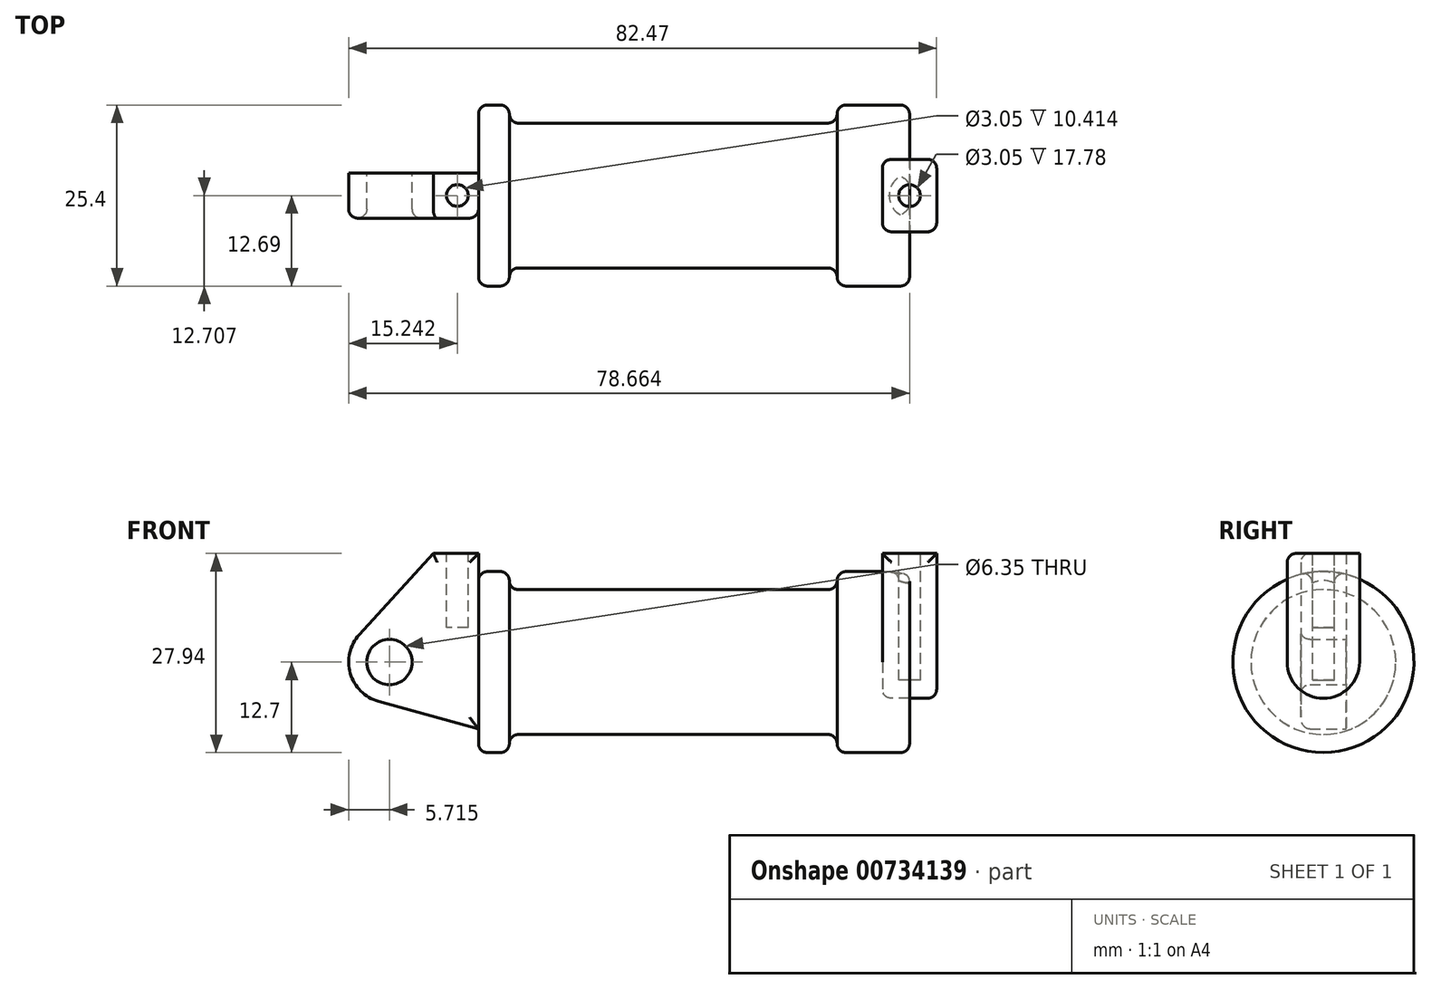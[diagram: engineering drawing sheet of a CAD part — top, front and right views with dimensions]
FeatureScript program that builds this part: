
annotation { "Feature Type Name" : "Feature", "Feature Type Description" : "" }
export const myFeature = defineFeature(function(context is Context, id is Id, definition is map)
    precondition{}
    {
        {
            var Q0;
            Q0=qCreatedBy(makeId("Front.planeOp"),FACE);
            var sketch = newSketch(context, id + "F0", { "sketchPlane" : qUnion([Q0])});
            skLineSegment(sketch, "E0", {"start": v(0, 0) * mm, "end": v(0, 12.7) * mm});
            skLineSegment(sketch, "E1", {"start": v(0, 12.7) * mm, "end": v(10.16, 12.7) * mm});
            skLineSegment(sketch, "E2", {"start": v(10.16, 12.7) * mm, "end": v(10.16, 10.16) * mm});
            skLineSegment(sketch, "E3", {"start": v(10.16, 10.16) * mm, "end": v(56.13, 10.16) * mm});
            skLineSegment(sketch, "E4", {"start": v(56.13, 10.16) * mm, "end": v(56.13, 12.7) * mm});
            skLineSegment(sketch, "E5", {"start": v(56.13, 12.7) * mm, "end": v(66.3, 12.7) * mm});
            skLineSegment(sketch, "E6", {"start": v(66.3, 12.7) * mm, "end": v(66.3, 0) * mm});
            skLineSegment(sketch, "E7", {"start": v(66.3, 0) * mm, "end": v(0, 0) * mm});
            skLineSegment(sketch, "E8", {"start": v(5.84, 15.24) * mm, "end": v(-0.5, 15.24) * mm});
            skLineSegment(sketch, "E9", {"start": v(-0.5, 15.24) * mm, "end": v(-10.88, 3.85) * mm});
            skLineSegment(sketch, "E10", {"start": v(0, 0) * mm, "end": v(-6.65, 0) * mm});
            skCircle(sketch, "E11", {"center": v(-6.65, 0) * mm, "radius": 5.72 * mm});
            skCircle(sketch, "E12", {"center": v(-6.65, 0) * mm, "radius": 3.18 * mm});
            skLineSegment(sketch, "E13", {"start": v(5.84, 15.24) * mm, "end": v(5.84, -9.4) * mm});
            skLineSegment(sketch, "E14", {"start": v(5.84, -9.4) * mm, "end": v(-8.18, -5.5) * mm});
            skSolve(sketch);
        }
        {
            var Q0;
            {var subQ0=sQuery(id+"F0.wireOp",EDGE,"E2");Q0=makeQuery(id+"F0.imprint","IMPRINT",FACE,{"disambiguationData":[TD([[makeQuery(id+"F0.imprint","IMPRINT",EDGE,{"derivedFrom":subQ0}),-1.0]])]});}
            var Q1;
            Q1=sQuery(id+"F0.wireOp",EDGE,"E7");
            revolve(context, id + "F1", {"surfaceOperationType" : NewSurfaceOperationType.NEW, "entities" : qUnion([Q0]), "axis" : qUnion([Q1]), "revolveType" : RevolveType.FULL});
        }
        {
            var Q0;
            {var subQ0=sQuery(id+"F0.wireOp",EDGE,"E14");Q0=makeQuery(id+"F0.imprint","IMPRINT",FACE,{"disambiguationData":[TD([[makeQuery(id+"F0.imprint","IMPRINT",EDGE,{"derivedFrom":subQ0}),-1.0]])]});}
            var Q1;
            {var subQ5=sQuery(id+"F0.wireOp",EDGE,"E12");Q1=makeQuery(id+"F0.imprint","IMPRINT",FACE,{"disambiguationData":[TD([[makeQuery(id+"F0.imprint","IMPRINT",EDGE,{"derivedFrom":subQ5}),-1.0]])]});}
            var Q2;
            {var subQ1=sQuery(id+"F0.wireOp",EDGE,"E0");Q2=makeQuery(id+"F0.imprint","IMPRINT",FACE,{"disambiguationData":[TD([[makeQuery(id+"F0.imprint","IMPRINT",EDGE,{"derivedFrom":subQ1}),1.0]])]});}
            var Q3;
            {var subQ0=sQuery(id+"F0.wireOp",EDGE,"E0");Q3=makeQuery(id+"F0.imprint","IMPRINT",FACE,{"disambiguationData":[TD([[makeQuery(id+"F0.imprint","IMPRINT",EDGE,{"derivedFrom":subQ0}),-1.0]])]});}
            extrude(context, id + "F2", {"entities" : qUnion([Q0, Q1, Q2, Q3]), "endBound" : BoundingType.SYMMETRIC, "depth" : 6.35 * mm, "offsetDistance" : 25.4 * mm});
        }
        {
            var Q0;
            Q0=makeQuery(id+"F1.opRevolve","SWEPT_FACE",FACE,{"disambiguationData":[OSD([sQuery(id+"F0.wireOp",EDGE,"E6")])]});
            var sketch = newSketch(context, id + "F3", { "sketchPlane" : qUnion([Q0])});
            skCircle(sketch, "E15", {"center": v(0, 0) * mm, "radius": 5.08 * mm});
            skCircle(sketch, "E16", {"center": v(0, 0) * mm, "radius": 1.52 * mm});
            skLineSegment(sketch, "E17", {"start": v(0, 0) * mm, "end": v(5.08, 0) * mm});
            skLineSegment(sketch, "E18", {"start": v(5.08, 0) * mm, "end": v(5.08, 15.24) * mm});
            skLineSegment(sketch, "E19", {"start": v(-0.4, 0) * mm, "end": v(-5.08, 0) * mm});
            skLineSegment(sketch, "E20", {"start": v(-5.08, 0) * mm, "end": v(-5.08, 15.24) * mm});
            skLineSegment(sketch, "E21", {"start": v(-5.08, 15.24) * mm, "end": v(5.08, 15.24) * mm});
            skSolve(sketch);
        }
        {
            var Q0;
            {var subQ0=sQuery(id+"F3.wireOp",EDGE,"E18");var subQ1=sQuery(id+"F3.wireOp",EDGE,"E15");var subQ2=makeQuery(id+"F3.imprint","INTERSECT",VERTEX,{"derivedFrom":[subQ1,sQuery(id+"F3.wireOp",EDGE,"E17"),subQ0]});Q0=makeQuery(id+"F3.imprint","IMPRINT",FACE,{"disambiguationData":[TD([[makeQuery(id+"F3.imprint","IMPRINT",EDGE,{"disambiguationData":[TD([[subQ2,-1.0]])],"derivedFrom":subQ1}),-1.0]])]});}
            var Q1;
            {var subQ0=sQuery(id+"F3.wireOp",EDGE,"E17");var subQ5=sQuery(id+"F3.wireOp",EDGE,"E16");var subQ6=makeQuery(id+"F3.imprint","INTERSECT",VERTEX,{"derivedFrom":[subQ5,subQ0]});Q1=makeQuery(id+"F3.imprint","IMPRINT",FACE,{"disambiguationData":[TD([[makeQuery(id+"F3.imprint","IMPRINT",EDGE,{"disambiguationData":[TD([[subQ6,-1.0]])],"derivedFrom":subQ5}),-1.0]])]});}
            var Q2;
            {var subQ0=sQuery(id+"F3.wireOp",EDGE,"E17");var subQ5=sQuery(id+"F3.wireOp",EDGE,"E16");var subQ6=makeQuery(id+"F3.imprint","INTERSECT",VERTEX,{"derivedFrom":[subQ5,subQ0]});Q2=makeQuery(id+"F3.imprint","IMPRINT",FACE,{"disambiguationData":[TD([[makeQuery(id+"F3.imprint","IMPRINT",EDGE,{"disambiguationData":[TD([[subQ6,1.0]])],"derivedFrom":subQ5}),-1.0]])]});}
            var Q3;
            {var subQ0=sQuery(id+"F3.wireOp",EDGE,"E21");Q3=makeQuery(id+"F3.imprint","IMPRINT",FACE,{"disambiguationData":[TD([[makeQuery(id+"F3.imprint","IMPRINT",EDGE,{"derivedFrom":subQ0}),-1.0]])]});}
            var Q4;
            {var subQ0=sQuery(id+"F3.wireOp",EDGE,"E16");var subQ1=makeQuery(id+"F3.imprint","INTERSECT",VERTEX,{"derivedFrom":[subQ0,sQuery(id+"F3.wireOp",EDGE,"E17")]});Q4=makeQuery(id+"F3.imprint","IMPRINT",FACE,{"disambiguationData":[TD([[makeQuery(id+"F3.imprint","IMPRINT",EDGE,{"disambiguationData":[TD([[subQ1,-1.0]])],"derivedFrom":subQ0}),1.0]])]});}
            extrude(context, id + "F4", {"entities" : qUnion([Q0, Q1, Q2, Q3, Q4]), "endBound" : BoundingType.SYMMETRIC, "depth" : 7.62 * mm, "offsetDistance" : 25.4 * mm});
        }
        {
            var Q0;
            Q0=makeQuery(id+"F4.opExtrude","SWEPT_FACE",FACE,{"disambiguationData":[OSD([sQuery(id+"F3.wireOp",EDGE,"E21")])]});
            var sketch = newSketch(context, id + "F5", { "sketchPlane" : qUnion([Q0])});
            skPoint(sketch, "E22.startSnap0", {"position": v(66.3, 5.08) * mm});
            skCircle(sketch, "E23", {"center": v(66.3, -0.01) * mm, "radius": 1.52 * mm});
            skCircle(sketch, "E24", {"center": v(2.87, 0) * mm, "radius": 1.52 * mm});
            skSolve(sketch);
        }
        {
            var Q0;
            Q0=makeQuery(id+"F5.imprint","IMPRINT",FACE,{"disambiguationData":[TD([[makeQuery(id+"F5.imprint","IMPRINT",EDGE,{"derivedFrom":sQuery(id+"F5.wireOp",EDGE,"E24")}),1.0]])]});
            var Q1;
            Q1 = qSketchRegion(id + "F7", true);
            extrude(context, id + "F6", {"entities" : qUnion([Q0, Q1]), "operationType" : NewBodyOperationType.REMOVE, "oppositeDirection" : true, "depth" : 10.4 * mm, "offsetDistance" : 25.4 * mm});
        }
        {
            var Q0;
            Q0=makeQuery(id+"F4.opExtrude","SWEPT_FACE",FACE,{"disambiguationData":[OSD([sQuery(id+"F3.wireOp",EDGE,"E21")])]});
            var sketch = newSketch(context, id + "F7", { "sketchPlane" : qUnion([Q0])});
            skSolve(sketch);
        }
        {
            var Q0;
            Q0=makeQuery(id+"F5.imprint","IMPRINT",FACE,{"disambiguationData":[TD([[makeQuery(id+"F5.imprint","IMPRINT",EDGE,{"derivedFrom":sQuery(id+"F5.wireOp",EDGE,"E23")}),1.0]])]});
            var Q1;
            Q1=sQuery(id+"F5.wireOp",EDGE,"E23");
            extrude(context, id + "F8", {"entities" : qUnion([Q0]), "operationType" : NewBodyOperationType.REMOVE, "surfaceEntities" : qUnion([Q1]), "oppositeDirection" : true, "depth" : 17.78 * mm, "offsetDistance" : 25.4 * mm});
        }
        {
            var Q0;
            Q0=makeQuery(id+"F1.opRevolve","SWEPT_FACE",FACE,{"disambiguationData":[OSD([sQuery(id+"F0.wireOp",EDGE,"E1")])]});
            var Q1;
            Q1=makeQuery(id+"F1.opRevolve","SWEPT_FACE",FACE,{"disambiguationData":[OSD([sQuery(id+"F0.wireOp",EDGE,"E3")])]});
            var Q2;
            Q2=makeQuery(id+"F1.opRevolve","SWEPT_FACE",FACE,{"disambiguationData":[OSD([sQuery(id+"F0.wireOp",EDGE,"E5")])]});
            var Q3;
            Q3=makeQuery(id+"F4.opExtrude","SWEPT_FACE",FACE,{"disambiguationData":[OSD([sQuery(id+"F3.wireOp",EDGE,"E20")])]});
            var Q4;
            Q4=makeQuery(id+"F4.opExtrude","SWEPT_FACE",FACE,{"disambiguationData":[OSD([sQuery(id+"F3.wireOp",EDGE,"E15")])]});
            var Q5;
            Q5=makeQuery(id+"F2.opExtrude","CAP_FACE",FACE,{"disambiguationData":[OSD([sQuery(id+"F0.wireOp",EDGE,"E8"),sQuery(id+"F0.wireOp",EDGE,"E9"),sQuery(id+"F0.wireOp",EDGE,"E11"),sQuery(id+"F0.wireOp",EDGE,"E12"),sQuery(id+"F0.wireOp",EDGE,"E13"),sQuery(id+"F0.wireOp",EDGE,"E14")])],"isStart":false});
            fillet(context, id + "F9", {"entities" : qUnion([Q0, Q1, Q2, Q3, Q4, Q5]), "radius" : 1.27 * mm, "tangentPropagation" : true, "allowEdgeOverflow" : false});
        }
    });
